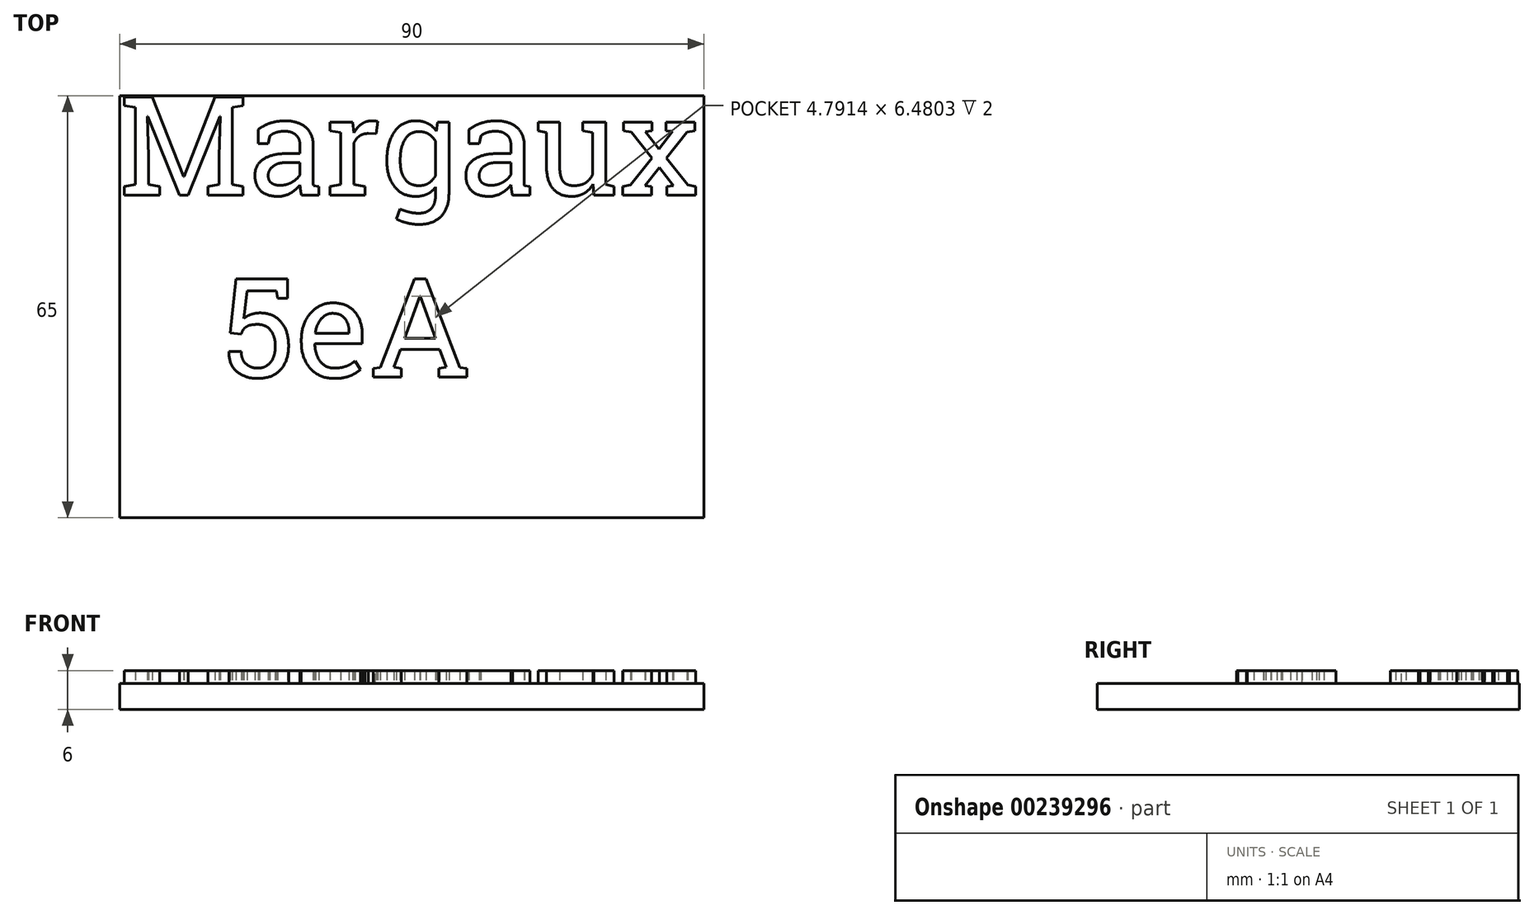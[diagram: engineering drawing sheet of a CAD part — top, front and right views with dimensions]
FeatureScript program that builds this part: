
annotation { "Feature Type Name" : "Feature", "Feature Type Description" : "" }
export const myFeature = defineFeature(function(context is Context, id is Id, definition is map)
    precondition{}
    {
        {
            var Q0;
            Q0=qCreatedBy(makeId("Top.planeOp"),FACE);
            var sketch = newSketch(context, id + "F0", { "sketchPlane" : qUnion([Q0])});
            skLineSegment(sketch, "E0.bottom", {"start": v(0, 0) * mm, "end": v(90, 0) * mm});
            skLineSegment(sketch, "E0.top", {"start": v(0, -65) * mm, "end": v(90, -65) * mm});
            skLineSegment(sketch, "E0.left", {"start": v(0, 0) * mm, "end": v(0, -65) * mm});
            skLineSegment(sketch, "E0.right", {"start": v(90, 0) * mm, "end": v(90, -65) * mm});
            skSolve(sketch);
        }
        {
            var Q0;
            Q0 = qSketchRegion(id + "FckT8R7pmecWqEm_0", true);
            var Q1;
            Q1=makeQuery(id+"F0.imprint","IMPRINT",FACE,{"disambiguationData":[TD([[makeQuery(id+"F0.imprint","IMPRINT",EDGE,{"derivedFrom":sQuery(id+"F0.wireOp",EDGE,"E0.bottom")}),-1.0]])]});
            extrude(context, id + "F1", {"entities" : qUnion([Q0, Q1]), "depth" : 4 * mm});
        }
        {
            var Q0;
            Q0=makeQuery(id+"F1.opExtrude","CAP_FACE",FACE,{"disambiguationData":[OSD([sQuery(id+"F0.wireOp",EDGE,"E0.bottom"),sQuery(id+"F0.wireOp",EDGE,"E0.top"),sQuery(id+"F0.wireOp",EDGE,"E0.left"),sQuery(id+"F0.wireOp",EDGE,"E0.right")])],"isStart":false});
            var sketch = newSketch(context, id + "F2", { "sketchPlane" : qUnion([Q0])});
            skText(sketch, "E1", { "text": "Margaux\n   5eA", "fontName": "RobotoSlab-Regular.ttf"});
            const initialGuessF2  = {"E1": [0, -0.01529, 1, 0, 0.01529]};
            skSetInitialGuess(sketch, initialGuessF2);
            skSolve(sketch);
        }
        {
            var Q0;
            Q0 = qSketchRegion(id + "F2", true);
            extrude(context, id + "F3", {"entities" : qUnion([Q0]), "operationType" : NewBodyOperationType.ADD, "depth" : 2 * mm});
        }
    });
